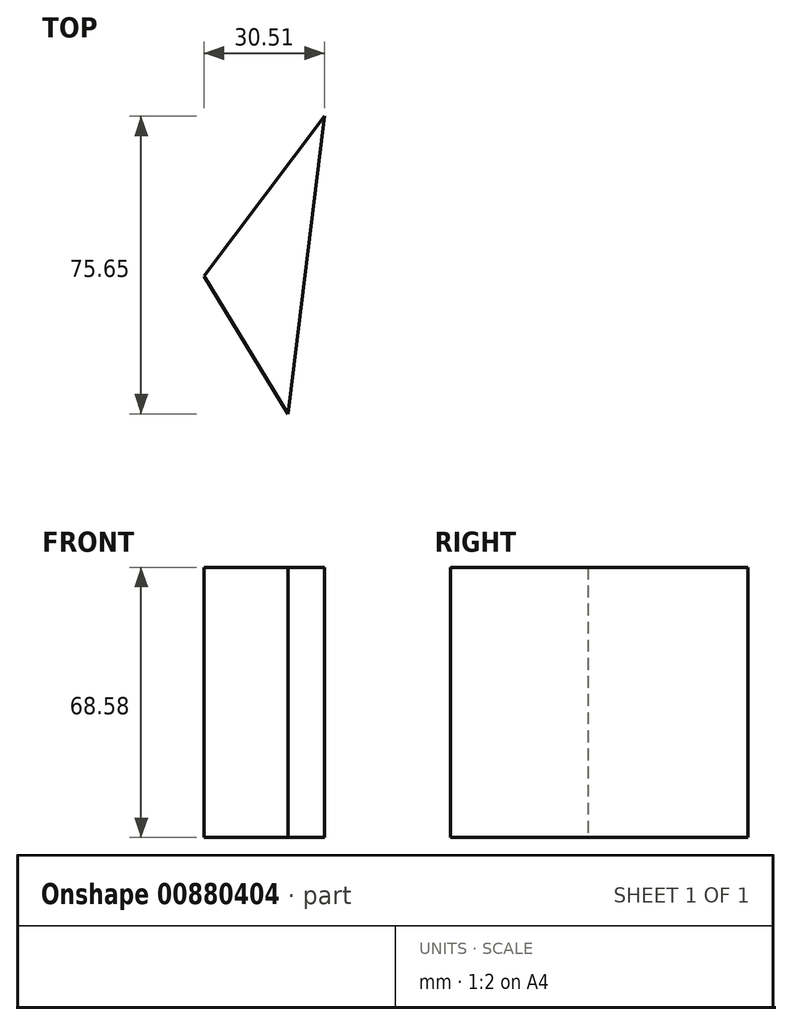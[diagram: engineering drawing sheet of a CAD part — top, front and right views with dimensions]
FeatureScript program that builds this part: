
annotation { "Feature Type Name" : "Feature", "Feature Type Description" : "" }
export const myFeature = defineFeature(function(context is Context, id is Id, definition is map)
    precondition{}
    {
        {
            var Q0;
            Q0=qCreatedBy(makeId("Top.planeOp"),FACE);
            var sketch = newSketch(context, id + "F0", { "sketchPlane" : qUnion([Q0])});
            skLineSegment(sketch, "E0", {"start": v(0, 0) * mm, "end": v(30.5, 40.62) * mm});
            skLineSegment(sketch, "E1", {"start": v(30.5, 40.62) * mm, "end": v(21.34, -35.03) * mm});
            skLineSegment(sketch, "E2", {"start": v(21.34, -35.03) * mm, "end": v(0, 0) * mm});
            skSolve(sketch);
        }
        {
            var Q0;
            Q0 = qSketchRegion(id + "F0", true);
            extrude(context, id + "F1", {"entities" : qUnion([Q0]), "depth" : 68.58 * mm, "offsetDistance" : 25.4 * mm});
        }
    });
